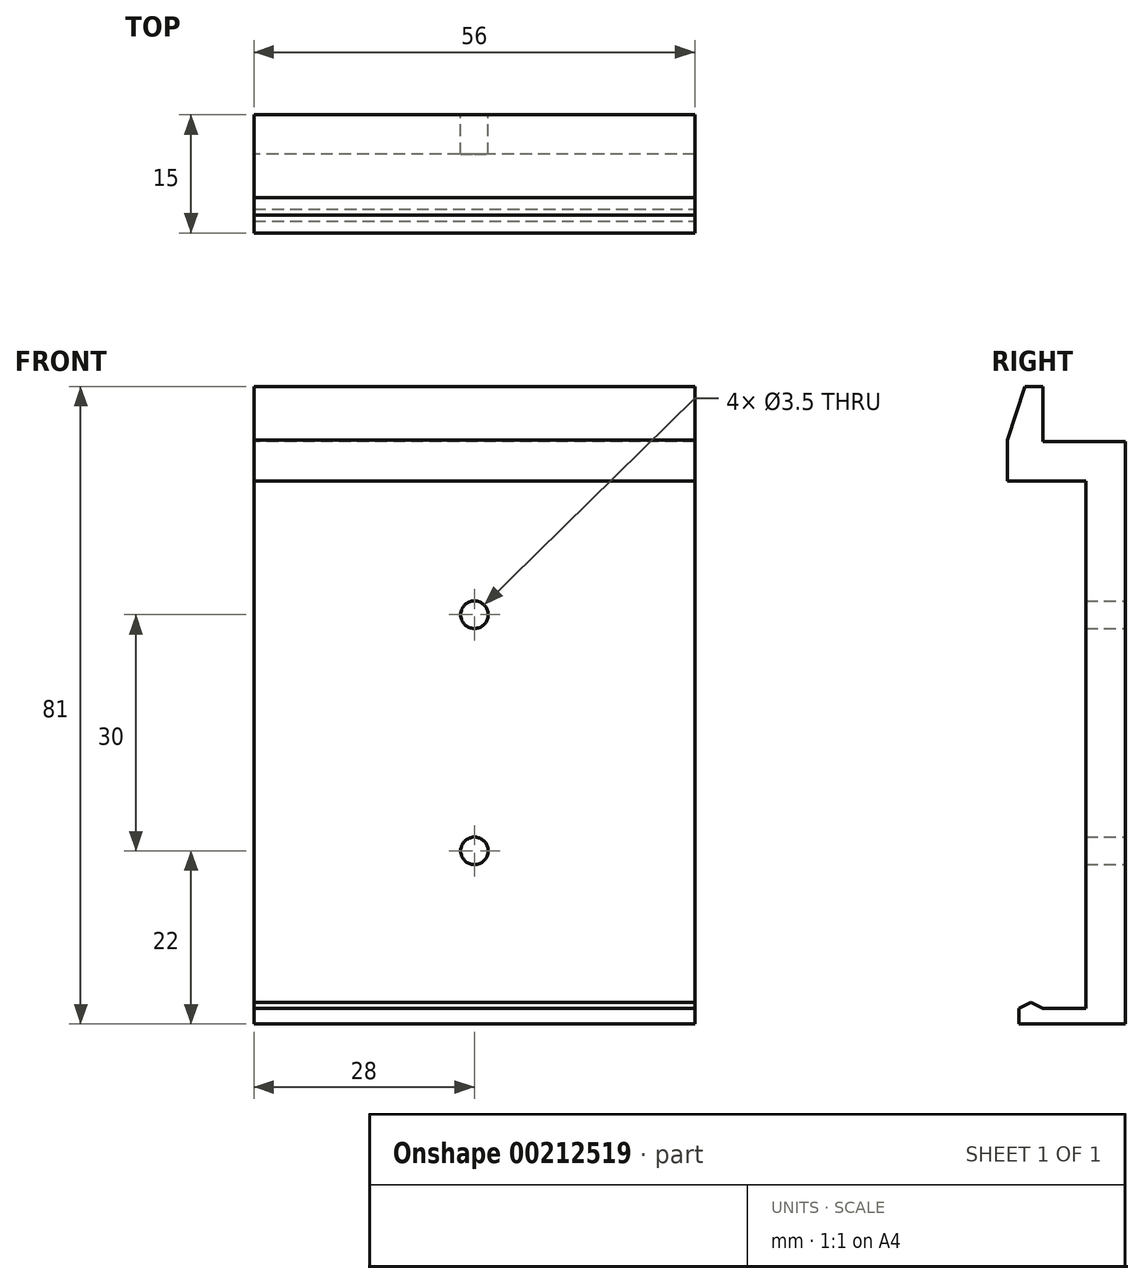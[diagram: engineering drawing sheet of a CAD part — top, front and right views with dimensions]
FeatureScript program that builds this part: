
annotation { "Feature Type Name" : "Feature", "Feature Type Description" : "" }
export const myFeature = defineFeature(function(context is Context, id is Id, definition is map)
    precondition{}
    {
        {
            var Q0;
            Q0=qCreatedBy(makeId("Right.planeOp"),FACE);
            var sketch = newSketch(context, id + "F0", { "sketchPlane" : qUnion([Q0])});
            skLineSegment(sketch, "E0", {"start": v(0, 0) * mm, "end": v(0, 67) * mm});
            skLineSegment(sketch, "E1", {"start": v(0, 67) * mm, "end": v(-10, 67) * mm});
            skLineSegment(sketch, "E2", {"start": v(-10, 67) * mm, "end": v(-10, 79) * mm});
            skLineSegment(sketch, "E3", {"start": v(-10, 79) * mm, "end": v(-5.5, 79) * mm});
            skLineSegment(sketch, "E4", {"start": v(-5.5, 79) * mm, "end": v(-5.5, 72) * mm});
            skLineSegment(sketch, "E5", {"start": v(-5.5, 72) * mm, "end": v(5, 72) * mm});
            skLineSegment(sketch, "E6", {"start": v(5, 72) * mm, "end": v(5, -2) * mm});
            skLineSegment(sketch, "E7", {"start": v(5, -2) * mm, "end": v(-8.5, -2) * mm});
            skLineSegment(sketch, "E8", {"start": v(-8.5, -2) * mm, "end": v(-8.5, 0.75) * mm});
            skLineSegment(sketch, "E9", {"start": v(-8.5, 0.75) * mm, "end": v(-5.5, 0.75) * mm});
            skLineSegment(sketch, "E10", {"start": v(-5.5, 0.75) * mm, "end": v(-5.5, 0) * mm});
            skLineSegment(sketch, "E11", {"start": v(-5.5, 0) * mm, "end": v(0, 0) * mm});
            skSolve(sketch);
        }
        {
            var Q0;
            Q0=makeQuery(id+"F0.imprint","IMPRINT",FACE,{"disambiguationData":[TD([[makeQuery(id+"F0.imprint","IMPRINT",EDGE,{"derivedFrom":sQuery(id+"F0.wireOp",EDGE,"E0")}),-1.0]])]});
            extrude(context, id + "F1", {"entities" : qUnion([Q0]), "depth" : 56 * mm});
        }
        {
            var Q0;
            Q0=makeQuery(id+"F1.opExtrude","CAP_FACE",FACE,{"disambiguationData":[OSD([sQuery(id+"F0.wireOp",EDGE,"E0"),sQuery(id+"F0.wireOp",EDGE,"E1"),sQuery(id+"F0.wireOp",EDGE,"E2"),sQuery(id+"F0.wireOp",EDGE,"E3"),sQuery(id+"F0.wireOp",EDGE,"E4"),sQuery(id+"F0.wireOp",EDGE,"E5"),sQuery(id+"F0.wireOp",EDGE,"E6"),sQuery(id+"F0.wireOp",EDGE,"E7"),sQuery(id+"F0.wireOp",EDGE,"E8"),sQuery(id+"F0.wireOp",EDGE,"E9"),sQuery(id+"F0.wireOp",EDGE,"E10"),sQuery(id+"F0.wireOp",EDGE,"E11")])],"isStart":false});
            var sketch = newSketch(context, id + "F2", { "sketchPlane" : qUnion([Q0])});
            skLineSegment(sketch, "E12", {"start": v(-7.75, 79) * mm, "end": v(-10, 79) * mm});
            skLineSegment(sketch, "E13", {"start": v(-10, 79) * mm, "end": v(-10, 72.18) * mm});
            skLineSegment(sketch, "E14", {"start": v(-10, 72.18) * mm, "end": v(-7.75, 79) * mm});
            skSolve(sketch);
        }
        {
            var Q0;
            Q0=makeQuery(id+"F2.imprint","IMPRINT",FACE,{"disambiguationData":[TD([[makeQuery(id+"F2.imprint","IMPRINT",EDGE,{"derivedFrom":sQuery(id+"F2.wireOp",EDGE,"E12")}),-1.0]])]});
            extrude(context, id + "F3", {"entities" : qUnion([Q0]), "operationType" : NewBodyOperationType.REMOVE, "oppositeDirection" : true, "depth" : 56 * mm});
        }
        {
            var Q0;
            Q0=makeQuery(id+"F1.opExtrude","CAP_FACE",FACE,{"disambiguationData":[OSD([sQuery(id+"F0.wireOp",EDGE,"E0"),sQuery(id+"F0.wireOp",EDGE,"E1"),sQuery(id+"F0.wireOp",EDGE,"E2"),sQuery(id+"F0.wireOp",EDGE,"E3"),sQuery(id+"F0.wireOp",EDGE,"E4"),sQuery(id+"F0.wireOp",EDGE,"E5"),sQuery(id+"F0.wireOp",EDGE,"E6"),sQuery(id+"F0.wireOp",EDGE,"E7"),sQuery(id+"F0.wireOp",EDGE,"E8"),sQuery(id+"F0.wireOp",EDGE,"E9"),sQuery(id+"F0.wireOp",EDGE,"E10"),sQuery(id+"F0.wireOp",EDGE,"E11")])],"isStart":false});
            var sketch = newSketch(context, id + "F4", { "sketchPlane" : qUnion([Q0])});
            skLineSegment(sketch, "E15", {"start": v(-8.5, 0) * mm, "end": v(-8.5, 0.75) * mm});
            skLineSegment(sketch, "E16", {"start": v(-8.5, 0.75) * mm, "end": v(-7, 0.75) * mm});
            skLineSegment(sketch, "E17", {"start": v(-7, 0.75) * mm, "end": v(-5.5, 0) * mm});
            skLineSegment(sketch, "E18", {"start": v(-5.5, 0) * mm, "end": v(-5.5, 0.75) * mm});
            skLineSegment(sketch, "E19", {"start": v(-5.5, 0.75) * mm, "end": v(-7, 0.75) * mm});
            skLineSegment(sketch, "E20", {"start": v(-8.5, 0) * mm, "end": v(-7, 0.75) * mm});
            skSolve(sketch);
        }
        {
            var Q0;
            Q0=makeQuery(id+"F4.imprint","IMPRINT",FACE,{"disambiguationData":[TD([[makeQuery(id+"F4.imprint","IMPRINT",EDGE,{"derivedFrom":sQuery(id+"F4.wireOp",EDGE,"E15")}),-1.0]])]});
            var Q1;
            Q1=makeQuery(id+"F4.imprint","IMPRINT",FACE,{"disambiguationData":[TD([[makeQuery(id+"F4.imprint","IMPRINT",EDGE,{"derivedFrom":sQuery(id+"F4.wireOp",EDGE,"E17")}),1.0]])]});
            extrude(context, id + "F5", {"entities" : qUnion([Q0, Q1]), "operationType" : NewBodyOperationType.REMOVE, "oppositeDirection" : true, "depth" : 56 * mm});
        }
        {
            var Q0;
            Q0=makeQuery(id+"F1.opExtrude","SWEPT_FACE",FACE,{"disambiguationData":[OSD([sQuery(id+"F0.wireOp",EDGE,"E6")])]});
            var sketch = newSketch(context, id + "F6", { "sketchPlane" : qUnion([Q0])});
            skLineSegment(sketch, "E21", {"start": v(-28, -2) * mm, "end": v(-28, 60.42) * mm, "construction": true});
            skLineSegment(sketch, "E22", {"start": v(-56, 35) * mm, "end": v(-28, 35) * mm, "construction": true});
            skLineSegment(sketch, "E23", {"start": v(-28, 35) * mm, "end": v(-28, 20) * mm, "construction": true});
            skLineSegment(sketch, "E24", {"start": v(-28, 20) * mm, "end": v(-28, 50) * mm, "construction": true});
            skCircle(sketch, "E25", {"center": v(-28, 50) * mm, "radius": 1.75 * mm});
            skCircle(sketch, "E26", {"center": v(-28, 20) * mm, "radius": 1.75 * mm});
            skSolve(sketch);
        }
        {
            var Q0;
            Q0=makeQuery(id+"F6.imprint","IMPRINT",FACE,{"disambiguationData":[TD([[makeQuery(id+"F6.imprint","IMPRINT",EDGE,{"derivedFrom":sQuery(id+"F6.wireOp",EDGE,"E25")}),1.0]])]});
            var Q1;
            Q1=makeQuery(id+"F6.imprint","IMPRINT",FACE,{"disambiguationData":[TD([[makeQuery(id+"F6.imprint","IMPRINT",EDGE,{"derivedFrom":sQuery(id+"F6.wireOp",EDGE,"E26")}),1.0]])]});
            extrude(context, id + "F7", {"entities" : qUnion([Q0, Q1]), "operationType" : NewBodyOperationType.REMOVE, "oppositeDirection" : true, "depth" : 5 * mm});
        }
        {
            var Q0;
            Q0=makeQuery(id+"F1.opExtrude","SWEPT_BODY",BODY,{"disambiguationData":[OSD([sQuery(id+"F0.wireOp",EDGE,"E0"),sQuery(id+"F0.wireOp",EDGE,"E1"),sQuery(id+"F0.wireOp",EDGE,"E2"),sQuery(id+"F0.wireOp",EDGE,"E3"),sQuery(id+"F0.wireOp",EDGE,"E4"),sQuery(id+"F0.wireOp",EDGE,"E5"),sQuery(id+"F0.wireOp",EDGE,"E6"),sQuery(id+"F0.wireOp",EDGE,"E7"),sQuery(id+"F0.wireOp",EDGE,"E8"),sQuery(id+"F0.wireOp",EDGE,"E9"),sQuery(id+"F0.wireOp",EDGE,"E10"),sQuery(id+"F0.wireOp",EDGE,"E11")])]});
            transform(context, id + "F8", {"entities" : qUnion([Q0]), "transformType" : TransformType.TRANSLATION_3D, "dx" : 0 * mm, "dy" : 0 * mm, "dz" : 0 * mm, "makeCopy" : true});
        }
    });
